# Revit family: Hose_Box-Two_Valves-Acorn-(8185-8186)-SSLF_Series
name_source: partatom
category: Plumbing Fixtures
units: mm (PartAtom-declared; Revit-internal decimal feet)

## family parameters
Cut with Voids When Loaded = Yes
Host = Face
OmniClass Number = 23.65.55.14
OmniClass Title = Valves for Liquid Services
Part Type = Normal
Room Calculation Point = No
Round Connector Dimension = Use Diameter
Shared = Yes

## types (2) — shared parameters
Assembly Code = D2010800
CW Connection = Yes
Default Elevation = 0"
Description = Hot and Cold Stainless Steel Hose Box with Waste Outlet
Finish = Stainless Steel-Acorn-Polished Satin
HW Connection = Yes
IAPMO Compliance = CUPC certified by IAPMO for U.S. and Canada
Installation Type = Wall Mounted
Manufacturer = Acorn
Material = Stainless Steel-Acorn-Polished Satin
NPT Connection Diameter = 3/4"
Product Documentation Link = https://www.acorneng.com
Product Page URL = https://www.acorneng.com
Type Comments = LEAD FREE STAINLESS STEEL RECESSED HOSE BOX HOT AND COLD
URL = https://www.acorneng.com
Vent Connection = No
Waste Connection = Yes
Waste Connection Diameter = 2"
Waste Fitting Material = Cast Bronze-Acorn-Rough Chrome
Width = 10 1/2"
cUPC Compliant = Yes
zero-valued in all types: CWFU, HWFU, WFU

## per-type parameters (varying)
| type | 8185-SSLF Hot & Cold Less Vacuum Breaker | 8186-SSLF Hot & Cold With Vacuum Breaker |
| 8185-SSLF | Yes | No |
| 8186-SSLF | No | Yes |

note: column(s) folded — value = type name in every type: Model

## geometry (parser evidence)
native form markers: Sweep x2
no freeform markers — native parametric forms only
